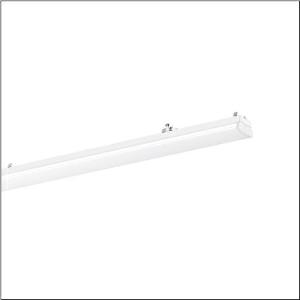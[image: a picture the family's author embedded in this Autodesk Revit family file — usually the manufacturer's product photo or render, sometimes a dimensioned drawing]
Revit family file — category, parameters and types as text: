
# Revit family: licross_r__21_recessed_opal_ho_52tl1ddn4e5m_042d
name_source: partatom
category: Lighting Fixtures
units: mm (PartAtom-declared; Revit-internal decimal feet)

## family parameters
Cut with Voids When Loaded = No
Host = Face
Light Source = No
Part Type = Normal
Room Calculation Point = No
Round Connector Dimension = Use Diameter
Shared = No

## types (1)
- --- (1 x LED, 14560 lm, 84.6 W, 4000K)
    Apparent Load = 85 VA
    CIE Flux Codes = 44 73 91 87 100
    Color Rendering = 80
    Color Temperature = 4000K
    Default Elevation = 1800 mm
    Description = Licross® 21 recessed opal HO, luminaire insert, of sheet steel, galvanised, coil coated, white, length: 1.500mm, width: 66mm, height: 67mm, LED rated luminous flux: 14.560lm, light colour: 840, control gear: DALI 2, with plug, 5-pole, with phase selection, mains connection: 220..240V, AC, 50/60Hz, rated input power: 85W, halogen-free wiring, primary optical cover: cover, of PMMA, light emission: direct with ceiling illumination distribution, primary light characteristic: symmetric, protection rating (complete): IP40, insulation class (complete): insulation class I (protective earthing), certification: CE, ENEC, VDE, UKCA, protection symbol: D if used in an environment without relevant dust loads with corresponding accessories, impact resistance: IK06, permissible ambient temperature for indoor applications: -25..+30°C, corresponds to IFS (International Featured Standards) requirements for safety and quality in the food industry, reducing of maximum allowable ambient temperature of 5°C with ceiling mounting, LABS conformity tested according to VDMA 24364:2018-05, packaging unit: 1 piece
    Height = 83 mm
    Lamp = 1 x LED
    Lamp Light Flux = 14560 lm
    Lamp Power = 84.6 W
    Lamp count = 1
    Length = 1500 mm
    Luminous efficacy = 172 lm/W
    Manufacturer = Siteco
    ModVariant = No
    Model = 52TL1DDN4E5M
    Mounting Place = Ceiling
    Mounting Type = Pendant
    Number of Poles = 1
    OnlyDefault = Yes
    Power Factor = 1
    Product Name = Licross® 21 recessed opal HO
    Product group = luminaire insert
    ProductGroupID = 901
    Protection Class = Protection class I
    Protection Degree = IP 40
    RLX_Detail_Level = 1
    RLX_Emergency_Light_Flux = 0 lm
    RLX_Emergency_Type = 0
    RLX_Emergency_Type_DB = No
    RlxData = <blob elided: 26965 chars, md5=41765690>
    Socket = socket
    Standby Power = 0 W
    System Light Flux = 14560 lm
    System Power = 85 W
    Type Comments = factory setting: luminous flux: 100 % | dim-lin: 254 | 484 mA
    Type Image = l_1313666.jpg
    URL = http://relux.com
    VarID = @adj_027131
    Voltage = 0 V
    Weight = 0.00 kg
    Width = 76 mm

## geometry (parser evidence)
native form markers: Blend x4, Sweep x16
no freeform markers — native parametric forms only
